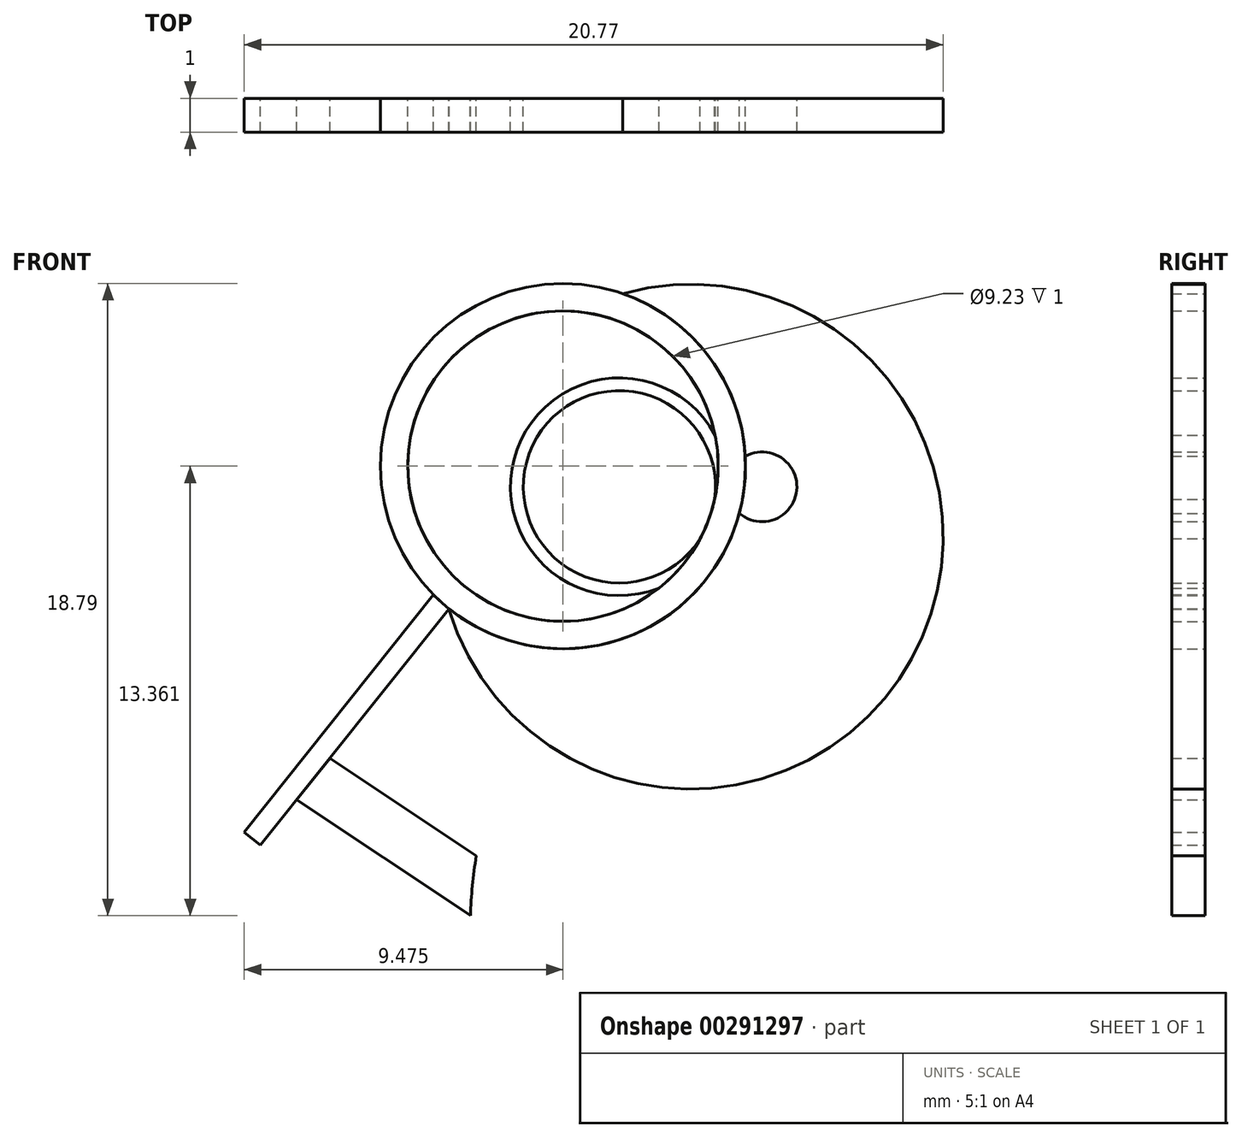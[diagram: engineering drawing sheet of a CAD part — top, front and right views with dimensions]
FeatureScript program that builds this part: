
annotation { "Feature Type Name" : "Feature", "Feature Type Description" : "" }
export const myFeature = defineFeature(function(context is Context, id is Id, definition is map)
    precondition{}
    {
        {
            var Q0;
            Q0=qCreatedBy(makeId("Front.planeOp"),FACE);
            var sketch = newSketch(context, id + "F0", { "sketchPlane" : qUnion([Q0])});
            skCircle(sketch, "E0", {"center": v(0, 18.26) * mm, "radius": 7.5 * mm});
            skArc(sketch, "E1", {"start": v(-5.1, 12.77) * mm, "mid": v(-6.56, 6.37) * mm, "end": v(-5, 0) * mm});
            skArc(sketch, "E2.MirrorCS", {"start": v(5.1, 12.77) * mm, "mid": v(6.56, 6.37) * mm, "end": v(5, 0) * mm});
            skLineSegment(sketch, "E3", {"start": v(-6.37, 8.78) * mm, "end": v(-10.96, 11.83) * mm});
            skLineSegment(sketch, "E4", {"start": v(-10.96, 11.83) * mm, "end": v(-11.83, 10.53) * mm});
            skLineSegment(sketch, "E5", {"start": v(-11.83, 10.53) * mm, "end": v(-6.56, 7.01) * mm});
            skPoint(sketch, "E5.endSnap0", {"position": v(-6.56, 6.37) * mm});
            skLineSegment(sketch, "E6", {"start": v(-5, 0) * mm, "end": v(5, 0) * mm});
            skCircle(sketch, "E7", {"center": v(-3.8, 20.36) * mm, "radius": 4.61 * mm});
            skCircle(sketch, "E8", {"center": v(-3.8, 20.36) * mm, "radius": 5.43 * mm});
            skLineSegment(sketch, "E9", {"start": v(-6.67, 16.76) * mm, "end": v(-12.79, 9.1) * mm});
            skLineSegment(sketch, "E10", {"start": v(-12.79, 9.1) * mm, "end": v(-13.27, 9.49) * mm});
            skLineSegment(sketch, "E11", {"start": v(-13.27, 9.49) * mm, "end": v(-7.13, 17.18) * mm});
            skArc(sketch, "E12.MirrorC", {"start": v(1.62, 20.66) * mm, "mid": v(3.15, 19.64) * mm, "end": v(1.45, 18.96) * mm});
            skArc(sketch, "E13", {"start": v(0.71, 19.37) * mm, "mid": v(-4.8, 20.73) * mm, "end": v(0.28, 18.2) * mm});
            skArc(sketch, "E14", {"start": v(0.72, 21.28) * mm, "mid": v(-5.16, 20.86) * mm, "end": v(-0.94, 16.74) * mm});
            skArc(sketch, "E15", {"start": v(1.39, 18.75) * mm, "mid": v(3.35, 19.62) * mm, "end": v(1.6, 20.87) * mm});
            skLineSegment(sketch, "E16", {"start": v(-6.56, 7.01) * mm, "end": v(-6.55, 7) * mm});
            skSolve(sketch);
        }
        {
            var Q0;
            {var subQ4=sQuery(id+"F0.wireOp",EDGE,"E15");Q0=makeQuery(id+"F0.imprint","IMPRINT",FACE,{"disambiguationData":[TD([[makeQuery(id+"F0.imprint","IMPRINT",EDGE,{"derivedFrom":subQ4}),-1.0]])]});}
            var Q1;
            {var subQ0=sQuery(id+"F0.wireOp",EDGE,"E13");Q1=makeQuery(id+"F0.imprint","IMPRINT",FACE,{"disambiguationData":[TD([[makeQuery(id+"F0.imprint","IMPRINT",EDGE,{"derivedFrom":subQ0}),1.0]])]});}
            var Q2;
            {var subQ5=sQuery(id+"F0.wireOp",EDGE,"E14");Q2=makeQuery(id+"F0.imprint","IMPRINT",FACE,{"disambiguationData":[TD([[makeQuery(id+"F0.imprint","IMPRINT",EDGE,{"derivedFrom":subQ5}),-1.0]])]});}
            var Q3;
            {var subQ0=sQuery(id+"F0.wireOp",EDGE,"E7");var subQ1=sQuery(id+"F0.wireOp",EDGE,"E0");var subQ2=makeQuery(id+"F0.imprint","INTERSECT",VERTEX,{"disambiguationData":[OD(0.0)],"derivedFrom":[subQ1,subQ0]});Q3=makeQuery(id+"F0.imprint","IMPRINT",FACE,{"disambiguationData":[TD([[makeQuery(id+"F0.imprint","IMPRINT",EDGE,{"disambiguationData":[TD([[subQ2,-1.0]])],"derivedFrom":subQ1}),-1.0]])]});}
            var Q4;
            {var subQ0=sQuery(id+"F0.wireOp",EDGE,"E4");Q4=makeQuery(id+"F0.imprint","IMPRINT",FACE,{"disambiguationData":[TD([[makeQuery(id+"F0.imprint","IMPRINT",EDGE,{"derivedFrom":subQ0}),-1.0]])]});}
            var Q5;
            {var subQ0=sQuery(id+"F0.wireOp",EDGE,"E4");Q5=makeQuery(id+"F0.imprint","IMPRINT",FACE,{"disambiguationData":[TD([[makeQuery(id+"F0.imprint","IMPRINT",EDGE,{"derivedFrom":subQ0}),1.0]])]});}
            var Q6;
            {var subQ0=sQuery(id+"F0.wireOp",EDGE,"E12.MirrorC");Q6=makeQuery(id+"F0.imprint","IMPRINT",FACE,{"disambiguationData":[TD([[makeQuery(id+"F0.imprint","IMPRINT",EDGE,{"derivedFrom":subQ0}),-1.0]])]});}
            extrude(context, id + "F1", {"entities" : qUnion([Q0, Q1, Q2, Q3, Q4, Q5, Q6]), "depth" : 1 * mm});
        }
        {
            var Q0;
            {var subQ0=sQuery(id+"F0.wireOp",EDGE,"E8");var subQ1=sQuery(id+"F0.wireOp",EDGE,"E0");var subQ2=makeQuery(id+"F0.imprint","INTERSECT",VERTEX,{"disambiguationData":[OD(0.0)],"derivedFrom":[subQ1,subQ0]});Q0=makeQuery(id+"F0.imprint","IMPRINT",FACE,{"disambiguationData":[TD([[makeQuery(id+"F0.imprint","IMPRINT",EDGE,{"disambiguationData":[TD([[subQ2,-1.0]])],"derivedFrom":subQ1}),-1.0]])]});}
            var Q1;
            {var subQ1=sQuery(id+"F0.wireOp",EDGE,"E8");var subQ8=sQuery(id+"F0.wireOp",EDGE,"E0");var subQ9=makeQuery(id+"F0.imprint","INTERSECT",VERTEX,{"disambiguationData":[OD(0.0)],"derivedFrom":[subQ8,subQ1]});Q1=makeQuery(id+"F0.imprint","IMPRINT",FACE,{"disambiguationData":[TD([[makeQuery(id+"F0.imprint","IMPRINT",EDGE,{"disambiguationData":[TD([[subQ9,-1.0]])],"derivedFrom":subQ8}),1.0]])]});}
            var Q2;
            {var subQ0=sQuery(id+"F0.wireOp",EDGE,"E2.MirrorCS");Q2=makeQuery(id+"F0.imprint","IMPRINT",FACE,{"disambiguationData":[TD([[makeQuery(id+"F0.imprint","IMPRINT",EDGE,{"derivedFrom":subQ0}),-1.0]])]});}
            var Q3;
            {var subQ5=sQuery(id+"F0.wireOp",EDGE,"E11");var subQ7=sQuery(id+"F0.wireOp",EDGE,"E0");var subQ9=makeQuery(id+"F0.imprint","INTERSECT",VERTEX,{"derivedFrom":[subQ7,subQ5]});Q3=makeQuery(id+"F0.imprint","IMPRINT",FACE,{"disambiguationData":[TD([[makeQuery(id+"F0.imprint","IMPRINT",EDGE,{"disambiguationData":[TD([[subQ9,-1.0]])],"derivedFrom":subQ7}),1.0]])]});}
            var Q4;
            {var subQ0=sQuery(id+"F0.wireOp",EDGE,"E11");var subQ1=sQuery(id+"F0.wireOp",EDGE,"E0");var subQ2=makeQuery(id+"F0.imprint","INTERSECT",VERTEX,{"derivedFrom":[subQ1,subQ0]});Q4=makeQuery(id+"F0.imprint","IMPRINT",FACE,{"disambiguationData":[TD([[makeQuery(id+"F0.imprint","IMPRINT",EDGE,{"disambiguationData":[TD([[subQ2,-1.0]])],"derivedFrom":subQ1}),-1.0]])]});}
            var Q5;
            {var subQ0=sQuery(id+"F0.wireOp",EDGE,"E7");var subQ1=sQuery(id+"F0.wireOp",EDGE,"E0");var subQ2=makeQuery(id+"F0.imprint","INTERSECT",VERTEX,{"disambiguationData":[OD(1.0)],"derivedFrom":[subQ1,subQ0]});Q5=makeQuery(id+"F0.imprint","IMPRINT",FACE,{"disambiguationData":[TD([[makeQuery(id+"F0.imprint","IMPRINT",EDGE,{"disambiguationData":[TD([[subQ2,-1.0]])],"derivedFrom":subQ1}),1.0]])]});}
            var Q6;
            {var subQ0=sQuery(id+"F0.wireOp",EDGE,"E16");Q6=makeQuery(id+"F0.imprint","IMPRINT",FACE,{"disambiguationData":[TD([[makeQuery(id+"F0.imprint","IMPRINT",EDGE,{"derivedFrom":subQ0}),1.0]])]});}
            extrude(context, id + "F2", {"entities" : qUnion([Q0, Q1, Q2, Q3, Q4, Q5, Q6]), "depth" : 1 * mm});
        }
        {
            var Q0;
            {var subQ0=sQuery(id+"F0.wireOp",EDGE,"E13");Q0=makeQuery(id+"F0.imprint","IMPRINT",FACE,{"disambiguationData":[TD([[makeQuery(id+"F0.imprint","IMPRINT",EDGE,{"derivedFrom":subQ0}),-1.0]])]});}
            var Q1;
            {var subQ0=sQuery(id+"F0.wireOp",EDGE,"E12.MirrorC");Q1=makeQuery(id+"F0.imprint","IMPRINT",FACE,{"disambiguationData":[TD([[makeQuery(id+"F0.imprint","IMPRINT",EDGE,{"derivedFrom":subQ0}),1.0]])]});}
            extrude(context, id + "F3", {"entities" : qUnion([Q0, Q1]), "depth" : 1 * mm});
        }
    });
